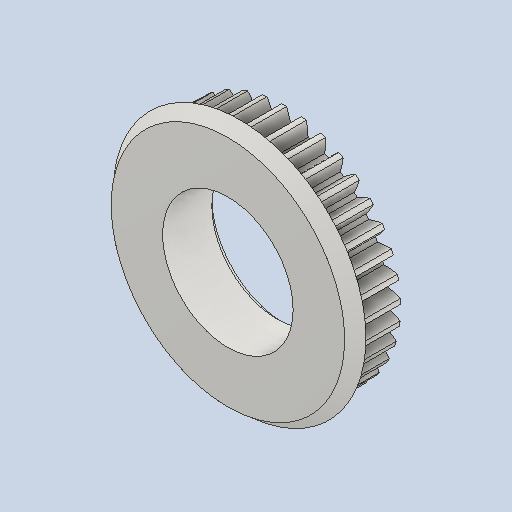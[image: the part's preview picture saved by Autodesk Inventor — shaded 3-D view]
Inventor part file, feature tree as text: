
AUTODESK INVENTOR PART (.ipt)
format: ipt  version: 2022 (Build 260153000, 153)  size: 620,032 bytes
history: native  units: in
note: dims shown in document units (in); Inventor stores cm internally (conversion verified against a paired STEP export)
features: other x12, sketch x4, plane x3
ambient origin geometry x8: Origin, YZ Plane, XZ Plane, XY Plane, X Axis, Y Axis, Z Axis, Center Point
bodies: Solid1 (feature_tree)
feature tree (19):
  other  "Spur Gear22_MIR.ipt"
  other  "Solid1::Spur Gear22_MIR.ipt"
  other  "TaggingFeature1"
  sketch  "Sketch1"  dims[d0=0.3937in]
  sketch  "Sketch2"  dims[d9=0.0in d14=0.0in d15=0.9352in d16=0.0in d17=0.0in d18=0.0in d19=0.9352in]
  sketch  "Sketch3"
  sketch  "Sketch4"
  plane  "XZ Plane_1"
  plane  "Work Plane2"
  plane  "Work Plane3"
  other  "Srf1"
  other  "Srf1::Derived"
  other  "Start plane iMate"
  other  "Distance iMate"
  other  "Position iMate"
  other  "Mesh iMate"
  other  "Axis iMate"
  other  "Mesh iMate2"
  other  "Align iMate"
